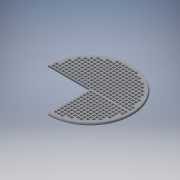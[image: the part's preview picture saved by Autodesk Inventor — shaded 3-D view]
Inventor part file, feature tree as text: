
AUTODESK INVENTOR PART (.ipt)
format: ipt  version: 2019 (Build 230136000, 136)  size: 1,861,632 bytes
history: native  units: mm
features: sketch x21, extrude x20, pattern_linear x6, other x4, projected_geometry x3, revolve x1, loft x1, shell x1, mirror x1
ambient origin geometry x8: Origin, YZ Plane, XZ Plane, XY Plane, X Axis, Y Axis, Z Axis, Center Point
bodies: Body1 (feature_tree)
feature tree (58):
  other  "полочка"
  revolve  "Вращение3"
  extrude  "Выдавливание103"  Depth=170.0mm
  sketch  "Эскиз4"
  other  "РабПлоскость1"
  sketch  "Эскиз5"
  loft  "Лофт1"
  extrude  "Выдавливание2"  Depth=17.0mm
  shell  "Оболочка1"  Thickness=4.0mm
  sketch  "Эскиз21"
  extrude  "Выдавливание16"  Depth=35.0mm
  other  "РабПлоскость7"
  sketch  "Эскиз23"
  extrude  "Выдавливание17"  TaperAngle=0.0deg  [1 undecoded]
  extrude  "Выдавливание18"  TaperAngle=0.0deg  [1 undecoded]
  extrude  "Выдавливание22"  TaperAngle=0.0deg  [1 undecoded]
  extrude  "Выдавливание24"  Depth=130.0mm TaperAngle=0.0deg
  extrude  "Выдавливание25"  Depth=5.0mm
  pattern_linear  "Прямоуг.массив1"  Spacing1=2.0mm  [1 undecoded]
  pattern_linear  "Прямоуг.массив2"  Spacing1=2.0mm  [1 undecoded]
  extrude  "Выдавливание26"  Depth=10.0mm TaperAngle=0.0deg
  pattern_linear  "Прямоуг.массив3"  Spacing1=143.802871mm  [1 undecoded]
  extrude  "Выдавливание27"  TaperAngle=0.0deg  [1 undecoded]
  pattern_linear  "Прямоуг.массив4"  Spacing1=1.0mm  [1 undecoded]
  extrude  "Выдавливание28"  Depth=30.0mm
  pattern_linear  "Прямоуг.массив5"  Spacing1=2.0mm  [1 undecoded]
  extrude  "Выдавливание29"  Depth=1.0mm TaperAngle=0.0deg
  pattern_linear  "Прямоуг.массив6"  Spacing1=14.0mm  [1 undecoded]
  mirror  "Зеркальное отражение7"
  extrude  "Выдавливание95"  Depth=14.0mm
  extrude  "Выдавливание96"  Depth=7.0mm
  extrude  "Выдавливание97"  Depth=10.0mm
  sketch  "Эскиз112"
  extrude  "Выдавливание98"  Depth=3.0mm
  extrude  "Выдавливание99"  Depth=3.0mm
  extrude  "Выдавливание100"  Depth=1.0mm TaperAngle=0.0deg
  extrude  "Выдавливание101"  Depth=14.0mm
  extrude  "Выдавливание102"  Depth=14.0mm
  sketch  "Эскиз6"
  projected_geometry  "Спроецированная петля1"
  sketch  "Эскиз26"
  sketch  "Эскиз28"
  sketch  "Эскиз29"
  sketch  "Эскиз30"
  sketch  "Эскиз31"
  sketch  "Эскиз32"
  sketch  "Эскиз33"
  sketch  "Эскиз109"
  sketch  "Эскиз110"
  sketch  "Эскиз111"
  projected_geometry  "Спроецированная петля42"
  sketch  "Эскиз114"
  projected_geometry  "Спроецированная петля43"
  sketch  "Эскиз115"
  sketch  "Эскиз116"
  sketch  "Эскиз118"
  other  "Твердое тело3"
  sketch  "Эскиз119"
note: 10 required parameter values undecoded (feature->parameter linkage not recoverable at this tier; creation-order binding heuristic only, values carry confidence <= 0.55)
